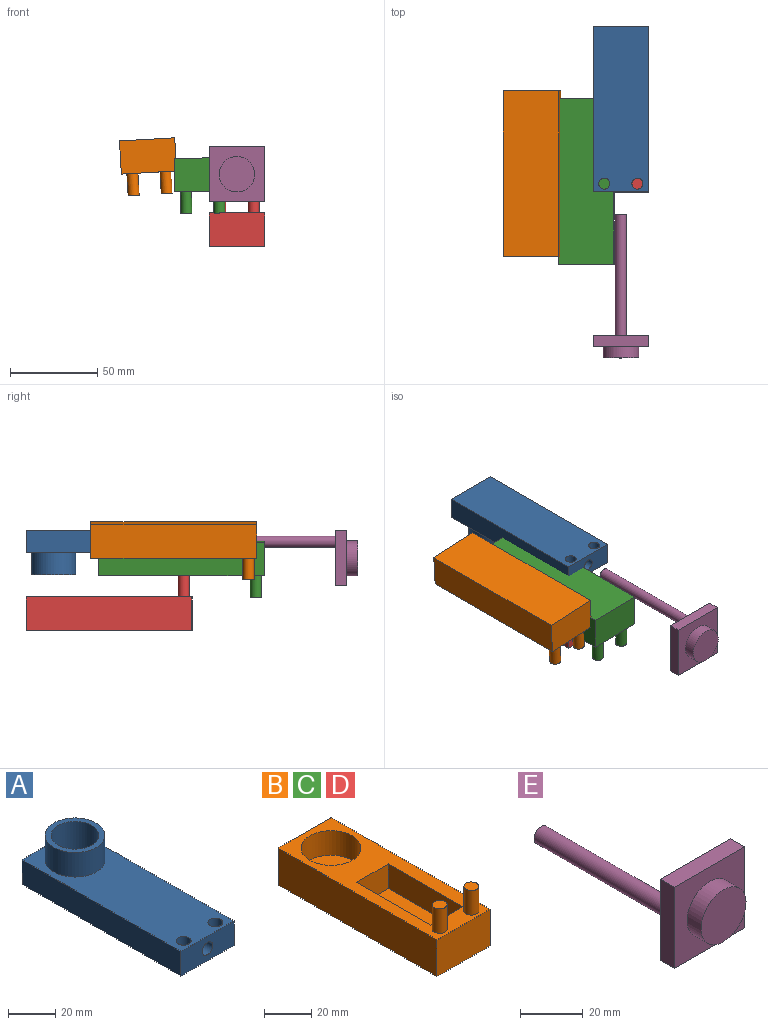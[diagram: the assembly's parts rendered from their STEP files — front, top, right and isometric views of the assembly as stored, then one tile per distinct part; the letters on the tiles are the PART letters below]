
ASSEMBLY  parts=5 mates=2
PART A: 13 faces, bbox 31.8x95.3x25.4 mm
  f0: plane 31.75x12.7mm, normal (0,-1,0), area 371.6mm2, adj f1,f3,f4,f5,f8
  f1: plane 95.25x12.7mm, normal (1,0,0), area 1209.7mm2, adj f0,f2,f4,f5
  f2: plane 31.75x12.7mm, normal (0,1,0), area 403.2mm2, adj f1,f3,f4,f5
  f3: plane 95.25x12.7mm, normal (-1,0,0), area 1209.7mm2, adj f0,f2,f4,f5
  f4: plane 95.25x31.75mm, normal (0,0,1), area 2454.1mm2, adj f0,f1,f2,f3,f10,f11,f12
  f5: plane 95.25x31.75mm, normal (0,0,-1), area 2960.8mm2, adj f0,f1,f2,f3,f11,f12
  f6: cylinder r=10.16mm len=22.23mm, axis (0,0,1), area 1386.7mm2, adj f7,f8,f9
  f7: plane 20.32x20.32mm, normal (0,0,1), area 324.3mm2, adj f6
  f8: cylinder r=3.17mm len=69.72mm, axis (0,-1,0), area 1385.8mm2, adj f0,f6
  f9: plane 25.4x25.4mm, normal (0,0,1), area 182.4mm2, adj f6,f10
  f10: cylinder r=12.7mm len=25.4mm, axis (0,0,-1), area 1013.4mm2, adj f4,f9
  f11: cylinder r=3.17mm len=12.7mm, axis (0,0,1), area 253.4mm2, adj f4,f5
  f12: cylinder r=3.17mm len=12.7mm, axis (0,0,1), area 253.4mm2, adj f4,f5
PART B: 17 faces, bbox 31.8x95.3x31.8 mm
  f0: plane 95.25x31.75mm, normal (0,0,1), area 1607.4mm2, adj f1,f2,f3,f4,f6,f8,f9,f10
  f1: plane 31.75x19.05mm, normal (0,-1,0), area 604.8mm2, adj f0,f2,f4,f5
  f2: plane 95.25x19.05mm, normal (1,0,0), area 1814.5mm2, adj f0,f1,f3,f5
  f3: plane 31.75x19.05mm, normal (0,1,0), area 604.8mm2, adj f0,f2,f4,f5
  f4: plane 95.25x19.05mm, normal (-1,0,0), area 1814.5mm2, adj f0,f1,f3,f5
  f5: plane 95.25x31.75mm, normal (0,0,-1), area 3024.2mm2, adj f1,f2,f3,f4
  f6: cylinder r=12.7mm len=25.4mm, axis (0,0,1), area 1013.4mm2, adj f0,f7
  f7: plane 25.4x25.4mm, normal (0,0,1), area 506.7mm2, adj f6
  f8: plane 19.05x12.7mm, normal (0,1,0), area 241.9mm2, adj f0,f9,f11,f12
  f9: plane 44.45x12.7mm, normal (-1,0,0), area 564.5mm2, adj f0,f8,f10,f12
  f10: plane 19.05x12.7mm, normal (0,-1,0), area 241.9mm2, adj f0,f9,f11,f12
  f11: plane 44.45x12.7mm, normal (1,0,0), area 564.5mm2, adj f0,f8,f10,f12
  f12: plane 44.45x19.05mm, normal (0,0,1), area 846.8mm2, adj f8,f9,f10,f11
  f13: cylinder r=3.17mm len=12.7mm, axis (0,0,-1), area 253.4mm2, adj f0,f14
  f14: plane 6.35x6.35mm, normal (0,0,1), area 31.7mm2, adj f13
  f15: cylinder r=3.17mm len=12.7mm, axis (0,0,-1), area 253.4mm2, adj f0,f16
  f16: plane 6.35x6.35mm, normal (0,0,1), area 31.7mm2, adj f15
PART C: same geometry as B
PART D: same geometry as B
PART E: 10 faces, bbox 31.8x82.6x31.8 mm
  f0: plane 31.75x31.75mm, normal (0,-1,0), area 683.8mm2, adj f1,f3,f4,f5,f6
  f1: plane 31.75x6.35mm, normal (1,0,0), area 201.6mm2, adj f0,f2,f4,f5
  f2: plane 31.75x31.75mm, normal (0,1,0), area 976.4mm2, adj f1,f3,f4,f5,f8
  f3: plane 31.75x6.35mm, normal (-1,0,0), area 201.6mm2, adj f0,f2,f4,f5
  f4: plane 31.75x6.35mm, normal (0,0,1), area 201.6mm2, adj f0,f1,f2,f3
  f5: plane 31.75x6.35mm, normal (0,0,-1), area 201.6mm2, adj f0,f1,f2,f3
  f6: cylinder r=10.16mm len=20.32mm, axis (0,1,0), area 405.4mm2, adj f0,f7
  f7: plane 20.32x20.32mm, normal (0,-1,0), area 324.3mm2, adj f6
  f8: cylinder r=3.17mm len=69.85mm, axis (0,-1,0), area 1393.4mm2, adj f2,f9
  f9: plane 6.35x6.35mm, normal (0,1,0), area 31.7mm2, adj f8
PLACE A rot(axis=(0,1,0),180deg) t=(11.09,27.32,61.48)mm
PLACE B rot(axis=(0,1,0),176.7deg) t=(10.65,-9.86,67.04)mm
PLACE C rot(axis=(0,1,0),179deg) t=(42.17,-14.13,55.4)mm
PLACE D t=(11.9,27.32,4.33)mm fixed
PLACE E rot(axis=(0,1,0),180deg) t=(-25.35,-61.58,61.48)mm
MATE slider E.f8 <-> A.f8  axis (0,-1,0) through (37.06,-33.01,55.13)mm
MATE slider A.f6 <-> D.f6  axis (0,0,1) through (37.06,59.07,36.08)mm
